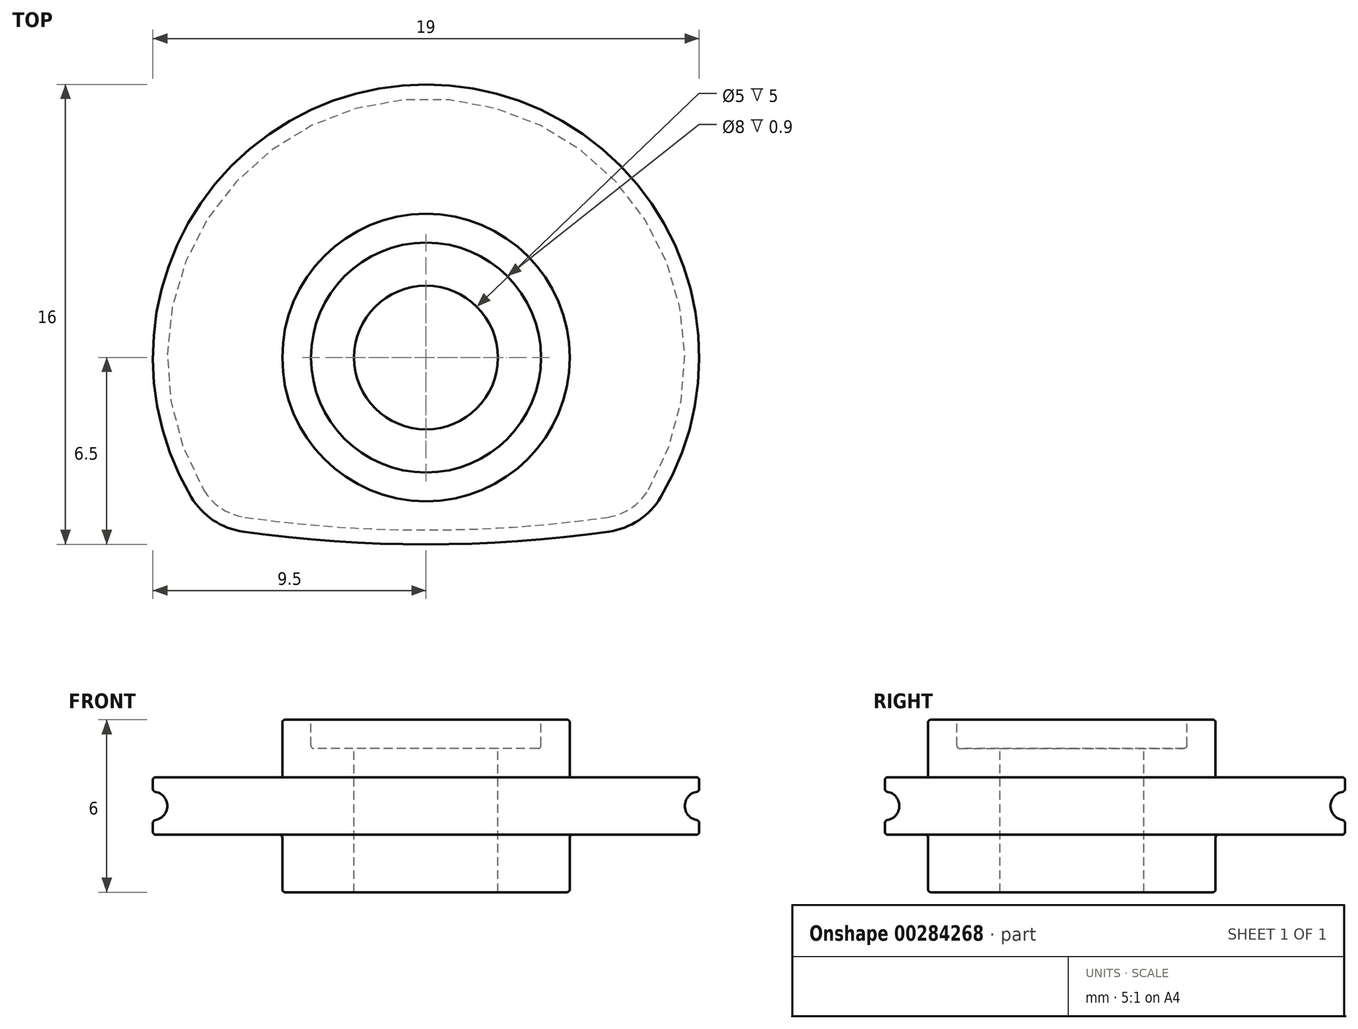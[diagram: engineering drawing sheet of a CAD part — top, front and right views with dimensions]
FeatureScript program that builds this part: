
annotation { "Feature Type Name" : "Feature", "Feature Type Description" : "" }
export const myFeature = defineFeature(function(context is Context, id is Id, definition is map)
    precondition{}
    {
        {
            assignVariable(context, id + "F0", {"name" : "Arm_width", "anyValue" : 2});
        }
        {
            assignVariable(context, id + "F1", {"name" : "Fillet", "anyValue" : 0.1});
        }
        {
            assignVariable(context, id + "F2", {"name" : "Screw_cap_depth", "anyValue" : 1});
        }
        {
            var Q0;
            Q0=qCreatedBy(makeId("Top.planeOp"),FACE);
            var sketch = newSketch(context, id + "F3", { "sketchPlane" : qUnion([Q0])});
            skCircle(sketch, "E0", {"center": v(0, 0) * mm, "radius": 5 * mm});
            skSolve(sketch);
        }
        {
            var Q0;
            Q0 = qSketchRegion(id + "F3", true);
            var Q1;
            Q1=makeQuery(id+"F3.imprint","IMPRINT",FACE,{"disambiguationData":[TD([[makeQuery(id+"F3.imprint","IMPRINT",EDGE,{"derivedFrom":sQuery(id+"F3.wireOp",EDGE,"lwzKTAft-k066-Xl6Z-xYGk-5HTUb5NTfGUl")}),1.0]])]});
            var Q2;
            Q2=makeQuery(id+"F3.imprint","IMPRINT",FACE,{"disambiguationData":[TD([[makeQuery(id+"F3.imprint","IMPRINT",EDGE,{"derivedFrom":sQuery(id+"F3.wireOp",EDGE,"e2zkgCW3-DaxK-HetB-FuQN-ffIRwnnk2RGx")}),1.0]])]});
            extrude(context, id + "F4", {"entities" : qUnion([Q0, Q1, Q2]), "depth" : 3 * mm, "offsetDistance" : 25 * mm, "hasSecondDirection" : true, "secondDirectionOppositeDirection" : true, "secondDirectionDepth" : 3 * mm});
        }
        {
            var Q0;
            Q0=qCreatedBy(makeId("Top.planeOp"),FACE);
            var sketch = newSketch(context, id + "F5", { "sketchPlane" : qUnion([Q0])});
            skArc(sketch, "E1", {"start": v(7.74, -4.6) * mm, "mid": v(0, 9) * mm, "end": v(-7.74, -4.6) * mm});
            skArc(sketch, "E2", {"start": v(-6.3, -5.56) * mm, "mid": v(0, -6) * mm, "end": v(6.3, -5.56) * mm});
            skPoint(sketch, "E3.visualSharp", {"position": v(7.18, -5.42) * mm});
            skArc(sketch, "E3.filletArc", {"start": v(6.3, -5.56) * mm, "mid": v(7.13, -5.24) * mm, "end": v(7.74, -4.6) * mm});
            skPoint(sketch, "E4.visualSharp", {"position": v(-7.18, -5.42) * mm});
            skArc(sketch, "E4.filletArc", {"start": v(-7.74, -4.6) * mm, "mid": v(-7.13, -5.24) * mm, "end": v(-6.3, -5.56) * mm});
            skSolve(sketch);
        }
        {
            var Q0;
            Q0=qCreatedBy(makeId("Top.planeOp"),FACE);
            var sketch = newSketch(context, id + "F6", { "sketchPlane" : qUnion([Q0]), "disableImprinting" : false});
            skCircle(sketch, "E5", {"center": v(0, 0) * mm, "radius": 10 * mm});
            skCircle(sketch, "E6", {"center": v(0, 0) * mm, "radius": 2.5 * mm});
            skSolve(sketch);
        }
        {
            var Q0;
            Q0 = qSketchRegion(id + "F6", true);
            extrude(context, id + "F7", {"entities" : qUnion([Q0]), "operationType" : NewBodyOperationType.ADD, "depth" : (getVariable(context, 'Arm_width') / 2) * mm, "offsetDistance" : 25 * mm, "hasSecondDirection" : true, "secondDirectionOppositeDirection" : true, "secondDirectionDepth" : (getVariable(context, 'Arm_width') / 2) * mm});
        }
        {
            var Q0;
            Q0=qCreatedBy(makeId("Front.planeOp"),FACE);
            var sketch = newSketch(context, id + "F8", { "sketchPlane" : qUnion([Q0])});
            skArc(sketch, "E7", {"start": v(9.42, 0.5) * mm, "mid": v(9, 0) * mm, "end": v(9.42, -0.5) * mm});
            skLineSegment(sketch, "E8", {"start": v(9.5, 0.9) * mm, "end": v(9.5, 0.6) * mm});
            skLineSegment(sketch, "E9.MirrorCS", {"start": v(9.5, -1.75) * mm, "end": v(9.5, -0.5) * mm});
            skLineSegment(sketch, "E10", {"start": v(0, 0) * mm, "end": v(0, 6.12) * mm, "construction": true});
            skLineSegment(sketch, "E11", {"start": v(8.5, 1) * mm, "end": v(9.4, 1) * mm});
            skPoint(sketch, "E12.newPointA", {"position": v(9.5, 1.75) * mm});
            skArc(sketch, "E12.filletArc", {"start": v(9.5, 0.9) * mm, "mid": v(9.47, 0.97) * mm, "end": v(9.4, 1) * mm});
            skLineSegment(sketch, "E13", {"start": v(8.5, 1) * mm, "end": v(8.5, 2) * mm});
            skLineSegment(sketch, "E14", {"start": v(8.5, 2) * mm, "end": v(18, 2) * mm});
            skLineSegment(sketch, "E15.MirrorCS", {"start": v(8.5, -2) * mm, "end": v(18, -2) * mm});
            skLineSegment(sketch, "E16.MirrorCS", {"start": v(8.5, -1) * mm, "end": v(8.5, -2) * mm});
            skLineSegment(sketch, "E17.MirrorCS", {"start": v(9.5, -0.9) * mm, "end": v(9.5, -0.6) * mm});
            skLineSegment(sketch, "E18.MirrorCS", {"start": v(8.5, -1) * mm, "end": v(9.4, -1) * mm});
            skArc(sketch, "E19.MirrorCS", {"start": v(9.5, -0.9) * mm, "mid": v(9.47, -0.97) * mm, "end": v(9.4, -1) * mm});
            skLineSegment(sketch, "E20", {"start": v(18, 2) * mm, "end": v(18, -2) * mm});
            skPoint(sketch, "E21.visualSharp", {"position": v(9.5, 0.5) * mm});
            skArc(sketch, "E21.filletArc", {"start": v(9.42, 0.5) * mm, "mid": v(9.48, 0.53) * mm, "end": v(9.5, 0.6) * mm});
            skPoint(sketch, "E22.visualSharp", {"position": v(9.5, -0.5) * mm});
            skArc(sketch, "E22.filletArc", {"start": v(9.5, -0.6) * mm, "mid": v(9.48, -0.53) * mm, "end": v(9.42, -0.5) * mm});
            skSolve(sketch);
        }
        {
            var Q0;
            Q0 = qSketchRegion(id + "F8", true);
            var Q1;
            Q1=sQuery(id+"F5.wireOp",EDGE,"E1");
            var Q2;
            Q2=sQuery(id+"F5.wireOp",EDGE,"E2");
            var Q3;
            Q3=sQuery(id+"F5.wireOp",EDGE,"E4.filletArc");
            var Q4;
            Q4=sQuery(id+"F5.wireOp",EDGE,"E3.filletArc");
            sweep(context, id + "F9", {"operationType" : NewBodyOperationType.REMOVE, "profiles" : qUnion([Q0]), "path" : qUnion([Q1, Q2, Q3, Q4])});
        }
        {
            var Q0;
            Q0=qCreatedBy(makeId("Top.planeOp"),FACE);
            var sketch = newSketch(context, id + "F10", { "sketchPlane" : qUnion([Q0])});
            skCircle(sketch, "E23", {"center": v(0, 0) * mm, "radius": 2.5 * mm});
            skSolve(sketch);
        }
        {
            var Q0;
            Q0 = qSketchRegion(id + "F10", true);
            extrude(context, id + "F11", {"entities" : qUnion([Q0]), "operationType" : NewBodyOperationType.REMOVE, "endBound" : BoundingType.THROUGH_ALL, "oppositeDirection" : true, "depth" : 25 * mm, "offsetDistance" : 25 * mm, "hasSecondDirection" : true, "secondDirectionBound" : BoundingType.THROUGH_ALL, "secondDirectionOppositeDirection" : false, "secondDirectionDepth" : 25 * mm});
        }
        {
            var Q0;
            Q0=makeQuery(id+"F4.opExtrude","CAP_FACE",FACE,{"disambiguationData":[OSD([sQuery(id+"F3.wireOp",EDGE,"E0")])],"isStart":false});
            var sketch = newSketch(context, id + "F12", { "sketchPlane" : qUnion([Q0])});
            skCircle(sketch, "E24", {"center": v(0, 0) * mm, "radius": 4 * mm});
            skSolve(sketch);
        }
        {
            var Q0;
            Q0 = qSketchRegion(id + "F12", true);
            extrude(context, id + "F13", {"entities" : qUnion([Q0]), "operationType" : NewBodyOperationType.REMOVE, "oppositeDirection" : true, "depth" : (getVariable(context, 'Screw_cap_depth')) * mm, "offsetDistance" : 25 * mm});
        }
        {
            var Q0;
            Q0=makeQuery(id+"F13.boolean.opBoolean","COPY",EDGE,{"derivedFrom":makeQuery(id+"F13.opExtrude","CAP_EDGE",EDGE,{"disambiguationData":[OSD([sQuery(id+"F12.wireOp",EDGE,"E24")])],"isStart":true})});
            var Q1;
            Q1=makeQuery(id+"F13.boolean.opBoolean","COPY",EDGE,{"derivedFrom":makeQuery(id+"F13.opExtrude","CAP_EDGE",EDGE,{"disambiguationData":[OSD([sQuery(id+"F12.wireOp",EDGE,"E24")])],"isStart":false})});
            var Q2;
            Q2=makeQuery(id+"F4.opExtrude","CAP_EDGE",EDGE,{"disambiguationData":[OSD([sQuery(id+"F3.wireOp",EDGE,"E0")])],"isStart":false});
            var Q3;
            Q3=makeQuery(id+"F7.boolean.opBoolean","INTERSECT",EDGE,{"derivedFrom":[makeQuery(id+"F4.opExtrude","SWEPT_FACE",FACE,{"disambiguationData":[OSD([sQuery(id+"F3.wireOp",EDGE,"E0")])]}),makeQuery(id+"F7.opExtrude","CAP_FACE",FACE,{"disambiguationData":[OSD([sQuery(id+"F6.wireOp",EDGE,"E5"),sQuery(id+"F6.wireOp",EDGE,"E6")])],"isStart":true})]});
            var Q4;
            Q4=makeQuery(id+"F4.opExtrude","CAP_EDGE",EDGE,{"disambiguationData":[OSD([sQuery(id+"F3.wireOp",EDGE,"E0")])],"isStart":true});
            fillet(context, id + "F14", {"entities" : qUnion([Q0, Q1, Q2, Q3, Q4]), "radius" : (getVariable(context, 'Fillet')) * mm, "tangentPropagation" : true, "allowEdgeOverflow" : false});
        }
    });
